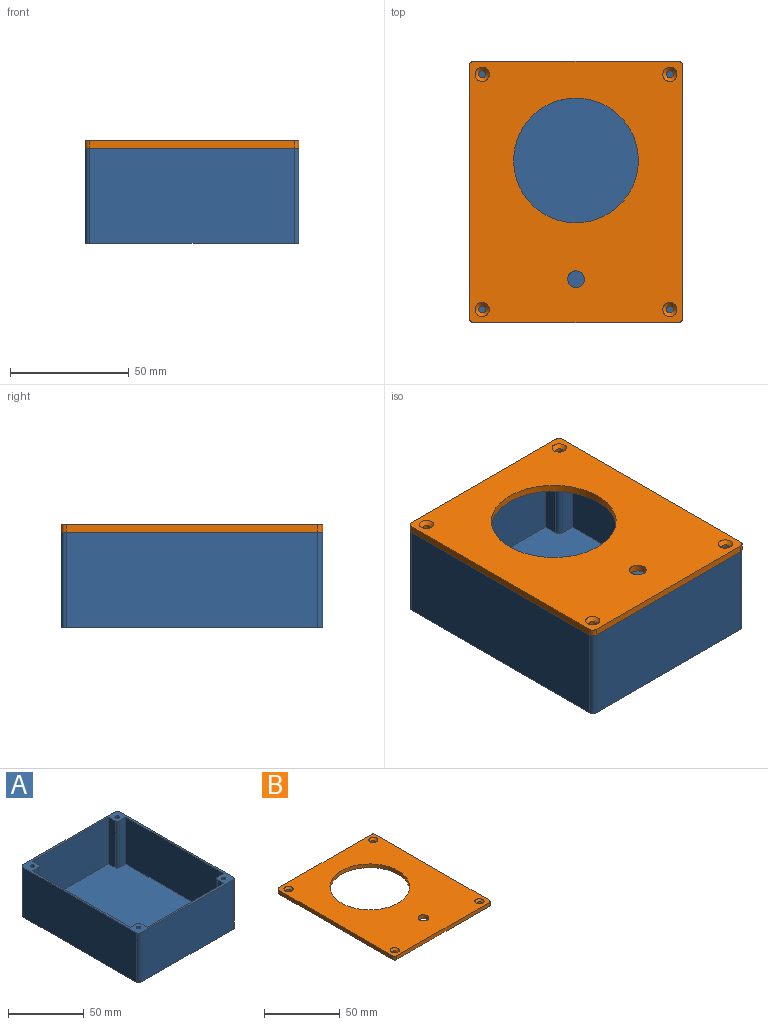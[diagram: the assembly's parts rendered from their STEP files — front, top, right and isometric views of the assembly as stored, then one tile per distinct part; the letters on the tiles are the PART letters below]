
ASSEMBLY  parts=2 mates=1
PART A: 35 faces, bbox 90x110x40 mm
  f0: plane 107x87mm, normal (0,0,1), area 9056.4mm2, adj f1,f2,f3,f4,f11,f12,f13,f14
  f1: plane 71x37.7mm, normal (0,1,0), area 2676.7mm2, adj f0,f5,f16,f18
  f2: plane 91x37.7mm, normal (-1,0,0), area 3430.7mm2, adj f0,f5,f13,f17
  f3: plane 71x37.7mm, normal (0,-1,0), area 2676.7mm2, adj f0,f5,f12,f14
  f4: plane 91x37.7mm, normal (1,0,0), area 3430.7mm2, adj f0,f5,f11,f15
  f5: plane 110x90mm, normal (0,0,1), area 811.9mm2, adj f1,f2,f3,f4,f6,f7,f8,f9
  f6: plane 86x40mm, normal (0,-1,0), area 3440mm2, adj f5,f10,f31,f34
  f7: plane 106x40mm, normal (1,0,0), area 4240mm2, adj f5,f10,f31,f32
  f8: plane 86x40mm, normal (0,1,0), area 3440mm2, adj f5,f10,f32,f33
  f9: plane 106x40mm, normal (-1,0,0), area 4240mm2, adj f5,f10,f33,f34
  f10: plane 110x90mm, normal (0,0,-1), area 9896.6mm2, adj f6,f7,f8,f9,f31,f32,f33,f34
  f11: plane 37.7x6mm, normal (0,-1,0), area 226.2mm2, adj f0,f4,f5,f30
  f12: plane 37.7x6mm, normal (1,0,0), area 226.2mm2, adj f0,f3,f5,f30
  f13: plane 37.7x6mm, normal (0,-1,0), area 226.2mm2, adj f0,f2,f5,f29
  f14: plane 37.7x6mm, normal (-1,0,0), area 226.2mm2, adj f0,f3,f5,f29
  f15: plane 37.7x6mm, normal (0,1,0), area 226.2mm2, adj f0,f4,f5,f28
  f16: plane 37.7x6mm, normal (1,0,0), area 226.2mm2, adj f0,f1,f5,f28
  f17: plane 37.7x6mm, normal (0,1,0), area 226.2mm2, adj f0,f2,f5,f27
  f18: plane 37.7x6mm, normal (-1,0,0), area 226.2mm2, adj f0,f1,f5,f27
  f19: cylinder r=1.5mm len=20mm, axis (0,0,1), area 188.5mm2, adj f5,f20
  f20: plane 3x3mm, normal (0,0,1), area 7.1mm2, adj f19
  f21: cylinder r=1.5mm len=20mm, axis (0,0,1), area 188.5mm2, adj f5,f22
  f22: plane 3x3mm, normal (0,0,1), area 7.1mm2, adj f21
  f23: cylinder r=1.5mm len=20mm, axis (0,0,1), area 188.5mm2, adj f5,f24
  f24: plane 3x3mm, normal (0,0,1), area 7.1mm2, adj f23
  f25: cylinder r=1.5mm len=20mm, axis (0,0,1), area 188.5mm2, adj f5,f26
  f26: plane 3x3mm, normal (0,0,1), area 7.1mm2, adj f25
  f27: cylinder r=2mm len=37.7mm, axis (0,0,1), area 118.4mm2, adj f0,f5,f17,f18
  f28: cylinder r=2mm len=37.7mm, axis (0,0,1), area 118.4mm2, adj f0,f5,f15,f16
  f29: cylinder r=2mm len=37.7mm, axis (0,0,1), area 118.4mm2, adj f0,f5,f13,f14
  f30: cylinder r=2mm len=37.7mm, axis (0,0,1), area 118.4mm2, adj f0,f5,f11,f12
  f31: cylinder r=2mm len=40mm, axis (0,0,1), area 125.7mm2, adj f5,f6,f7,f10
  f32: cylinder r=2mm len=40mm, axis (0,0,-1), area 125.7mm2, adj f5,f7,f8,f10
  f33: cylinder r=2mm len=40mm, axis (0,0,1), area 125.7mm2, adj f5,f8,f9,f10
  f34: cylinder r=2mm len=40mm, axis (0,0,-1), area 125.7mm2, adj f5,f6,f9,f10
PART B: 20 faces, bbox 90x110x3 mm
  f0: plane 86x3mm, normal (0,1,0), area 258mm2, adj f4,f5,f14,f17
  f1: plane 106x3mm, normal (-1,0,0), area 318mm2, adj f4,f5,f14,f15
  f2: plane 86x3mm, normal (0,-1,0), area 258mm2, adj f4,f5,f15,f16
  f3: plane 106x3mm, normal (1,0,0), area 318mm2, adj f4,f5,f16,f17
  f4: plane 110x90mm, normal (0,0,1), area 7580.2mm2, adj f0,f1,f2,f3,f10,f11,f12,f13
  f5: plane 110x90mm, normal (0,0,-1), area 7665.1mm2, adj f0,f1,f2,f3,f6,f7,f8,f9
  f6: cylinder r=1.5mm len=3mm, axis (0,0,1), area 14.1mm2, adj f5,f13
  f7: cylinder r=1.5mm len=3mm, axis (0,0,1), area 14.1mm2, adj f5,f10
  f8: cylinder r=1.5mm len=3mm, axis (0,0,1), area 14.1mm2, adj f5,f11
  f9: cylinder r=1.5mm len=3mm, axis (0,0,1), area 14.1mm2, adj f5,f12
  f10: cone r=1.5mm half-angle=45deg, axis (0,0,1), area 30mm2, adj f4,f7
  f11: cone r=1.5mm half-angle=45deg, axis (0,0,1), area 30mm2, adj f4,f8
  f12: cone r=1.5mm half-angle=45deg, axis (0,0,1), area 30mm2, adj f4,f9
  f13: cone r=1.5mm half-angle=45deg, axis (0,0,1), area 30mm2, adj f4,f6
  f14: cylinder r=2mm len=3mm, axis (0,0,1), area 9.4mm2, adj f0,f1,f4,f5
  f15: cylinder r=2mm len=3mm, axis (0,0,-1), area 9.4mm2, adj f1,f2,f4,f5
  f16: cylinder r=2mm len=3mm, axis (0,0,1), area 9.4mm2, adj f2,f3,f4,f5
  f17: cylinder r=2mm len=3mm, axis (0,0,-1), area 9.4mm2, adj f0,f3,f4,f5
  f18: cylinder r=26.25mm len=52.5mm, axis (0,0,1), area 494.8mm2, adj f4,f5
  f19: cylinder r=3.5mm len=7mm, axis (0,0,1), area 66mm2, adj f4,f5
PLACE A at identity fixed
PLACE B t=(2.12,151.41,40)mm
MATE slider A.f25 <-> B.f8  axis (0,0,1) through (-39.5,-49.5,40)mm
